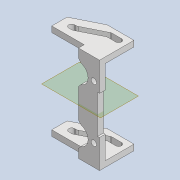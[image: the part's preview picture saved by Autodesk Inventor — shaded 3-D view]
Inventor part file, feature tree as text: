
AUTODESK INVENTOR PART (.ipt)
format: ipt  version: 2020 (Build 240168000, 168)  size: 300,544 bytes
history: native  units: mm
features: extrude x7, sketch x7, thicken_offset x6, projected_geometry x5, other x4, reference x3, fillet x1, plane x1, mirror x1, chamfer x1
ambient origin geometry x8: Origin, YZ Plane, XZ Plane, XY Plane, X Axis, Y Axis, Z Axis, Center Point
bodies: Solid1 (feature_tree)
feature tree (36):
  extrude  "Extrusion1"  Depth=25.0mm
  extrude  "Extrusion3"  Depth=1.5mm
  thicken_offset  "Thicken3"
  extrude  "Extrusion4"  Depth=1.5mm TaperAngle=0.0deg
  fillet  "Fillet1"  Radius=3.0mm
  thicken_offset  "Thicken4"
  thicken_offset  "Thicken5"
  thicken_offset  "Thicken6"
  extrude  "Extrusion5"  Depth=1.5mm
  extrude  "Extrusion6"  Depth=2.5mm
  plane  "Work Plane1"
  mirror  "Mirror1"
  extrude  "Extrusion7"  Depth=1.5mm TaperAngle=0.0deg
  extrude  "Extrusion8"  Depth=1.5mm
  thicken_offset  "Thicken7"
  thicken_offset  "Thicken8"
  chamfer  "Chamfer1"  Distance=1.5mm
  sketch  "Sketch1"  dims[d0=5.0mm d1=25.0mm]
  reference  "Reference1"
  sketch  "Sketch3"  dims[d2=1.5mm d3=0.0mm d16=12.0mm]
  projected_geometry  "Projected Loop2"
  sketch  "Sketch5"  dims[d17=6.0mm d18=1.5mm d19=0.0mm d20=3.0mm d21=2.0mm]
  reference  "Reference3"
  reference  "Reference4"
  sketch  "Sketch6"  dims[d22=1.5mm d23=0.8mm]
  projected_geometry  "Projected Loop3"
  sketch  "Sketch7"  dims[d24=1.5mm d25=2.5mm]
  projected_geometry  "Projected Loop4"
  sketch  "Sketch8"  dims[d26=1.5mm d27=1.5mm d28=0.0mm]
  projected_geometry  "Projected Loop5"
  sketch  "Sketch9"  dims[d29=1.0mm d30=1.5mm d31=1.5mm d32=1.5mm d33=1.5mm d34=1.5mm d35=1.5mm d36=1.5mm d37=1.2mm d38=4.0mm d39=3.0mm d40=1.5mm d41=4.0mm d42=3.0mm d43=1.5mm d44=0.0mm d45=1.5mm d46=1.4mm d47=1.5mm d48=1.4mm d49=1.5mm d50=0.0mm d51=1.5mm d52=0.0mm d53=7.0mm d54=300.0mm d55=0.0mm d56=0.5mm d57=0.5mm d58=0.5mm d59=0.5mm d60=0.7mm d61=2.0mm d62=45.0deg]
  projected_geometry  "Projected Loop6"
  parser-record x1  (decoder bookkeeping rows leaked as tree rows — omitted from the tree; the rows remain in map.json)
  other  "dock_ass_1.iam"
  other  "dock_p_1:1"
  other  "dock_pin_1:1"
note: 1 file-system path scrubbed to <path> (originals preserved in map.json)
